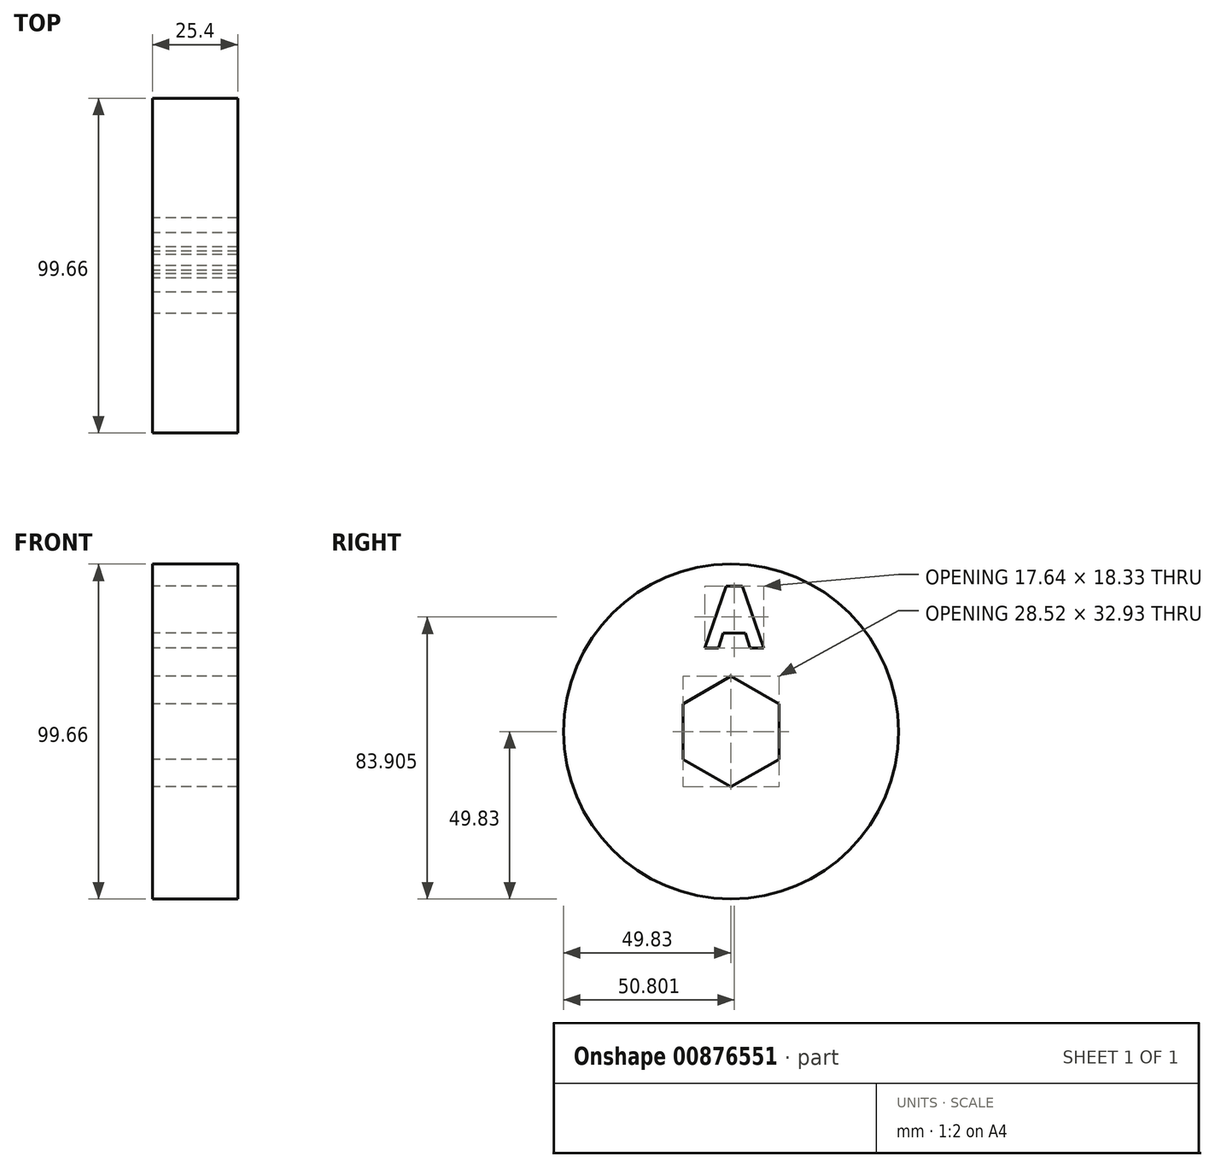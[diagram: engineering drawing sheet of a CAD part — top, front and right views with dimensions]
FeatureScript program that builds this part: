
annotation { "Feature Type Name" : "Feature", "Feature Type Description" : "" }
export const myFeature = defineFeature(function(context is Context, id is Id, definition is map)
    precondition{}
    {
        {
            var Q0;
            Q0=qCreatedBy(makeId("Right.planeOp"),FACE);
            var sketch = newSketch(context, id + "F0", { "sketchPlane" : qUnion([Q0])});
            skCircle(sketch, "E0", {"center": v(0, 0) * mm, "radius": 49.83 * mm});
            skCircle(sketch, "E1.cCircle", {"center": v(0, 0) * mm, "radius": 14.26 * mm, "construction": true});
            skLineSegment(sketch, "E1.0", {"start": v(14.26, 8.23) * mm, "end": v(14.26, -8.23) * mm});
            skLineSegment(sketch, "E1.1", {"start": v(14.26, -8.23) * mm, "end": v(0, -16.47) * mm});
            skLineSegment(sketch, "E1.2", {"start": v(0, -16.47) * mm, "end": v(-14.26, -8.23) * mm});
            skLineSegment(sketch, "E1.3", {"start": v(-14.26, -8.23) * mm, "end": v(-14.26, 8.23) * mm});
            skLineSegment(sketch, "E1.4", {"start": v(-14.26, 8.23) * mm, "end": v(0, 16.47) * mm});
            skLineSegment(sketch, "E1.5", {"start": v(0, 16.47) * mm, "end": v(14.26, 8.23) * mm});
            skPoint(sketch, "E1.0.midPoint", {"position": v(14.26, 0) * mm});
            skText(sketch, "E2", { "text": "A", "fontName": "OpenSans-Bold.ttf"});
            const initialGuessF0  = {"E2": [-0.00785, 0.02491, 1, 0, 0.01841]};
            skSetInitialGuess(sketch, initialGuessF0);
            skSolve(sketch);
        }
        {
            var Q0;
            Q0 = qSketchRegion(id + "F0", true);
            extrude(context, id + "F1", {"entities" : qUnion([Q0]), "depth" : 25.4 * mm, "offsetDistance" : 25.4 * mm});
        }
    });
